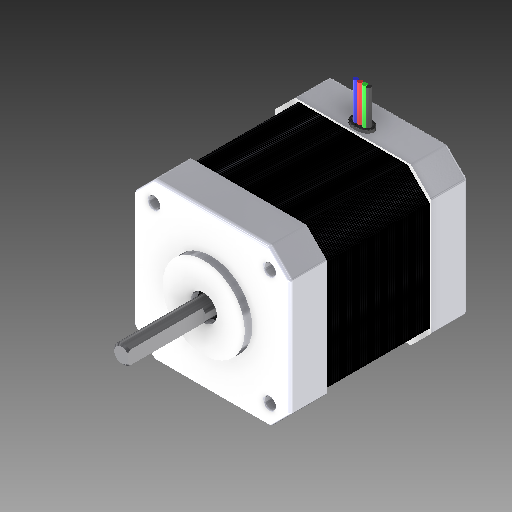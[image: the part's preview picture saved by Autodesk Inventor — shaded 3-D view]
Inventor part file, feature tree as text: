
AUTODESK INVENTOR PART (.ipt)
format: ipt  version: 2018 (Build 220112000, 112)  size: 1,182,720 bytes
history: native  units: mm
features: extrude x13, sketch x5, hole x4, fillet x4, chamfer x2, plane x1, pattern_linear x1, projected_geometry x1
ambient origin geometry x8: Origin, YZ Plane, XZ Plane, XY Plane, X Axis, Y Axis, Z Axis, Center Point
bodies: Solid1 (feature_tree)
feature tree (31):
  sketch  "Sketch1"  dims[d0=7.0mm d1=22.0mm]
  extrude  "Extrusion1"  Depth=22.0mm
  extrude  "Extrusion2"  Depth=31.0mm
  extrude  "Extrusion3"  Depth=3.0mm
  plane  "Work Plane2"
  extrude  "Extrusion7"  Depth=3.0mm
  extrude  "Extrusion8"  Depth=10.0mm
  chamfer  "Chamfer1"  Distance=42.0mm
  pattern_linear  "Rectangular Pattern2"  Spacing1=135.0deg  [1 undecoded]
  hole  "Hole1"  [1 undecoded]
  hole  "Hole2"  [1 undecoded]
  hole  "Hole3"  [1 undecoded]
  hole  "Hole4"  [1 undecoded]
  extrude  "Extrusion9"  Depth=10.0mm TaperAngle=0.0deg
  fillet  "Fillet1"  Radius=2.0mm
  fillet  "Fillet2"  Radius=48.0mm
  chamfer  "Chamfer2"  [1 undecoded]
  fillet  "Fillet3"  Radius=28.0mm
  sketch  "Sketch6"  dims[d10=3.0mm d11=3.0mm]
  extrude  "Extrusion10"  Depth=10.0mm
  fillet  "Fillet4"  Radius=1.0mm
  extrude  "Extrusion11"  Depth=10.0mm
  extrude  "Extrusion12"  Depth=10.0mm
  extrude  "Extrusion13"  Depth=10.0mm
  extrude  "Extrusion14"  Depth=10.0mm
  extrude  "Extrusion15"  Depth=10.0mm
  extrude  "Extrusion16"  Depth=10.0mm
  sketch  "Sketch4"  dims[d4=5.0mm d5=31.0mm]
  projected_geometry  "Projected Loop2"
  sketch  "Sketch5"  dims[d6=31.0mm d9=3.0mm]
  sketch  "Sketch11"  dims[d12=3.0mm d39=42.0mm d40=42.0mm d41=135.0deg d42=51.618795mm d43=51.618795mm d44=25.809398mm d45=25.809398mm d46=24.0mm d47=0.0mm d48=2.0mm d49=0.0mm d50=48.0mm d51=0.0mm d60=-10.0mm d126=28.0mm d127=0.0mm d128=1.0mm d129=1.0mm d130=1.0mm d131=1.0mm d132=0.5mm d134=0.5mm d135=0.5mm d136=0.5mm d137=0.5mm d138=1.0mm d139=1.0mm d140=0.5mm d141=0.0mm d145=0.125mm d146=2.0mm d147=45.0deg d148=560.0mm d150=0.5mm d151=10.0mm d152=10.0mm d153=6.0mm d154=6.0mm d155=4.0mm d156=2.0mm d157=90.0deg d158=3.0mm d159=0.0mm d160=10.0mm d161=10.0mm d162=6.0mm d163=6.0mm d164=4.0mm d165=2.0mm d166=90.0deg d167=3.0mm d168=0.0mm d169=10.0mm d170=10.0mm d171=6.0mm d172=6.0mm d173=4.0mm d174=2.0mm d175=90.0deg d176=3.0mm d177=0.0mm d178=10.0mm d179=10.0mm d180=6.0mm d181=6.0mm d182=4.0mm d183=2.0mm d184=90.0deg d185=3.0mm d186=0.0mm d187=48.0mm d188=0.0mm d189=47.0mm d190=0.0mm d191=1.0mm d192=1.0mm d193=0.5mm d194=2.0mm d195=45.0deg d196=0.5mm d197=1.2mm d198=40.0mm d200=1.2mm d201=10.0mm d203=10.0mm d205=2.5mm d206=2.5mm d207=1.0mm d208=0.0mm d209=0.3mm d210=10.0mm d211=0.0mm d212=10.0mm d213=0.0mm d214=10.0mm d215=0.0mm d216=10.0mm d217=0.0mm d218=0.2mm d219=5.0mm d220=0.0mm d221=0.0mm d225=20.0mm d226=0.0mm]
note: 6 required parameter values undecoded (feature->parameter linkage not recoverable at this tier; creation-order binding heuristic only, values carry confidence <= 0.55)
